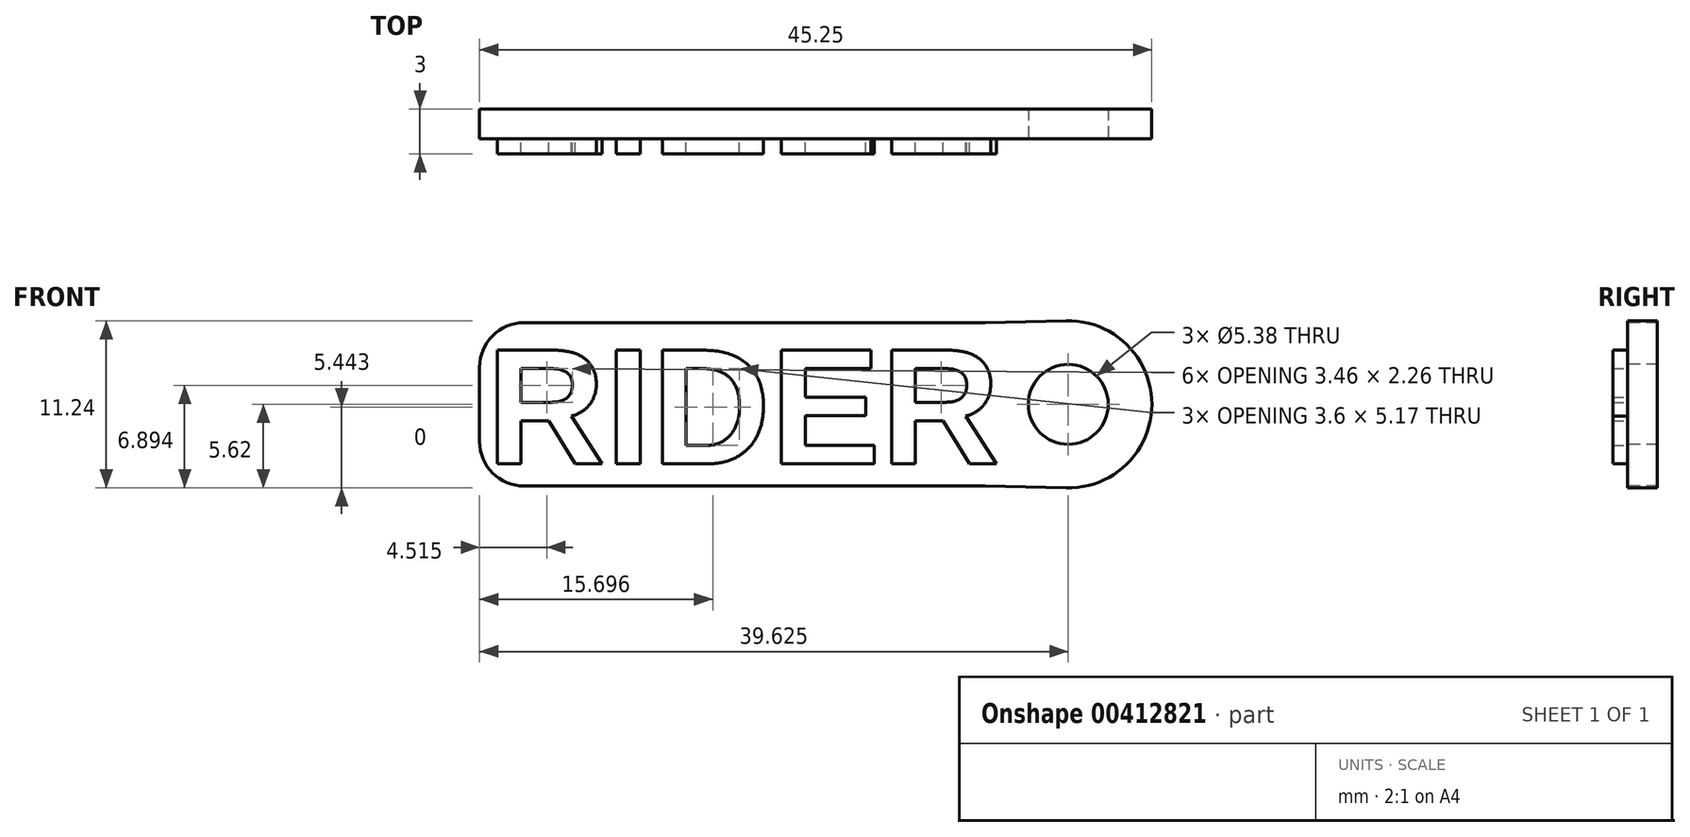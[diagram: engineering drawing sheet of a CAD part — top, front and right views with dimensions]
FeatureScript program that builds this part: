
annotation { "Feature Type Name" : "Feature", "Feature Type Description" : "" }
export const myFeature = defineFeature(function(context is Context, id is Id, definition is map)
    precondition{}
    {
        {
            var Q0;
            Q0=qCreatedBy(makeId("Front.planeOp"),FACE);
            var sketch = newSketch(context, id + "F0", { "sketchPlane" : qUnion([Q0])});
            skText(sketch, "E0", { "text": "RIDER", "fontName": "Arimo-Bold.ttf"});
            const initialGuessF0  = {"E0": [-0.01756, -0.008, 1, 0, 0.008]};
            skSetInitialGuess(sketch, initialGuessF0);
            skSolve(sketch);
        }
        {
            var Q0;
            Q0=qSketchRegion(id+"F0",true);
            extrude(context, id + "F1", {"entities" : qUnion([Q0]), "depth" : 1 * mm});
        }
        {
            var Q0;
            Q0=qCreatedBy(makeId("Front.planeOp"),FACE);
            var sketch = newSketch(context, id + "F2", { "sketchPlane" : qUnion([Q0])});
            skLineSegment(sketch, "E1", {"start": v(16, -9.5) * mm, "end": v(-18, -9.5) * mm});
            skLineSegment(sketch, "E2", {"start": v(-18, 1.5) * mm, "end": v(16, 1.5) * mm});
            skLineSegment(sketch, "E3", {"start": v(16, -9.5) * mm, "end": v(16, 1.5) * mm, "construction": true});
            skLineSegment(sketch, "E4", {"start": v(-18, -9.5) * mm, "end": v(-18, 1.5) * mm});
            skCircle(sketch, "E5", {"center": v(21.62, -4) * mm, "radius": 5.62 * mm});
            skLineSegment(sketch, "E6", {"start": v(16, -4) * mm, "end": v(67.35, -4) * mm, "construction": true});
            skPoint(sketch, "E6.endSnap0", {"position": v(16, -4) * mm});
            skLineSegment(sketch, "E7", {"start": v(16, 1.5) * mm, "end": v(21.5, 1.62) * mm});
            skLineSegment(sketch, "E8", {"start": v(21.5, -9.62) * mm, "end": v(16, -9.5) * mm});
            skCircle(sketch, "E9", {"center": v(21.62, -4) * mm, "radius": 2.69 * mm});
            skSolve(sketch);
        }
        {
            var Q0;
            Q0=qSketchRegion(id+"F2",true);
            extrude(context, id + "F3", {"entities" : qUnion([Q0]), "oppositeDirection" : true, "depth" : 2 * mm});
        }
        {
            var Q0;
            Q0=makeQuery(id+"F3.opExtrude","SWEPT_EDGE",EDGE,{"disambiguationData":[OSD([sQuery(id+"F2.wireOp",EDGE,"E2"),sQuery(id+"F2.wireOp",EDGE,"E4")])]});
            var Q1;
            Q1=makeQuery(id+"F3.opExtrude","SWEPT_EDGE",EDGE,{"disambiguationData":[OSD([sQuery(id+"F2.wireOp",EDGE,"E1"),sQuery(id+"F2.wireOp",EDGE,"E4")])]});
            var Q2;
            Q2=makeQuery(id+"F3.opExtrude","SWEPT_EDGE",EDGE,{"disambiguationData":[OSD([sQuery(id+"F2.wireOp",EDGE,"E1"),sQuery(id+"F2.wireOp",EDGE,"E8")])]});
            var Q3;
            Q3=makeQuery(id+"F3.opExtrude","SWEPT_EDGE",EDGE,{"disambiguationData":[OSD([sQuery(id+"F2.wireOp",EDGE,"E2"),sQuery(id+"F2.wireOp",EDGE,"E7")])]});
            fillet(context, id + "F4", {"entities" : qUnion([Q0, Q1, Q2, Q3]), "radius" : 3 * mm, "tangentPropagation" : true, "allowEdgeOverflow" : false});
        }
    });
